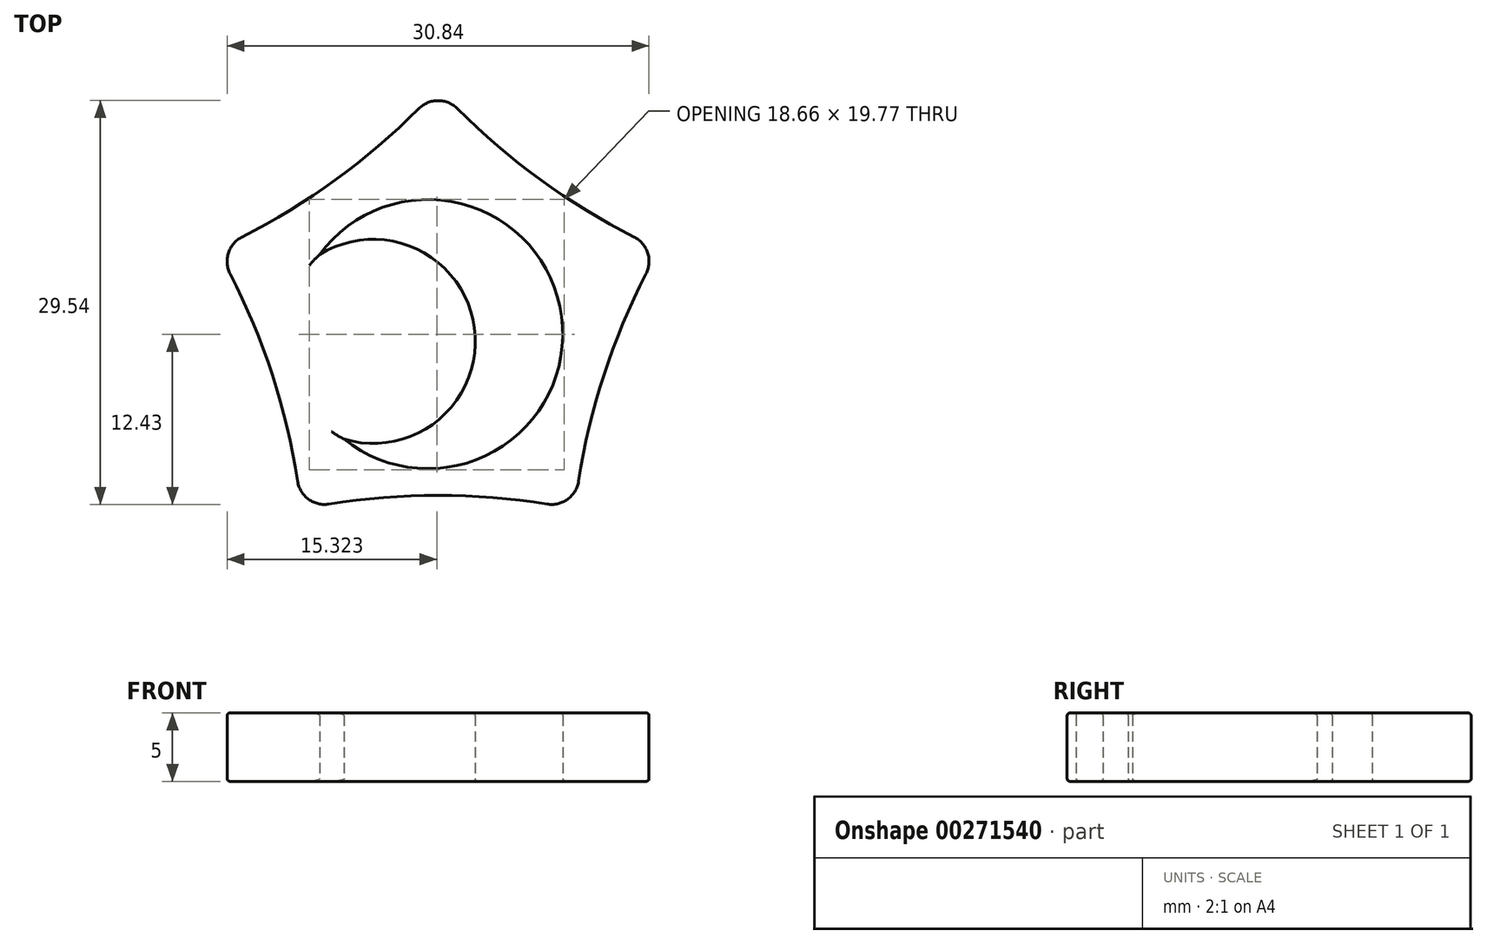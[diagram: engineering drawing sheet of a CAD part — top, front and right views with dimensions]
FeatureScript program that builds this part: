
annotation { "Feature Type Name" : "Feature", "Feature Type Description" : "" }
export const myFeature = defineFeature(function(context is Context, id is Id, definition is map)
    precondition{}
    {
        {
            var Q0;
            Q0=qCreatedBy(makeId("Top.planeOp"),FACE);
            var sketch = newSketch(context, id + "F0", { "sketchPlane" : qUnion([Q0])});
            skCircle(sketch, "E0.cCircle", {"center": v(0, 0) * mm, "radius": 13.76 * mm, "construction": true});
            skLineSegment(sketch, "E0.0", {"start": v(10, -13.76) * mm, "end": v(-10, -13.76) * mm});
            skLineSegment(sketch, "E0.1", {"start": v(-10, -13.76) * mm, "end": v(-16.18, 5.26) * mm});
            skLineSegment(sketch, "E0.2", {"start": v(-16.18, 5.26) * mm, "end": v(0, 17.01) * mm});
            skLineSegment(sketch, "E0.3", {"start": v(0, 17.01) * mm, "end": v(16.18, 5.26) * mm});
            skLineSegment(sketch, "E0.4", {"start": v(16.18, 5.26) * mm, "end": v(10, -13.76) * mm});
            skPoint(sketch, "E0.0.midPoint", {"position": v(0, -13.76) * mm});
            skArc(sketch, "E1", {"start": v(-16.18, 5.26) * mm, "mid": v(-7.5, 10.32) * mm, "end": v(0, 17.01) * mm});
            skArc(sketch, "E2", {"start": v(-10, -13.76) * mm, "mid": v(-12.13, -3.94) * mm, "end": v(-16.18, 5.26) * mm});
            skArc(sketch, "E3", {"start": v(10, -13.76) * mm, "mid": v(0, -12.75) * mm, "end": v(-10, -13.76) * mm});
            skArc(sketch, "E4", {"start": v(16.18, 5.26) * mm, "mid": v(12.13, -3.94) * mm, "end": v(10, -13.76) * mm});
            skArc(sketch, "E5", {"start": v(0, 17.01) * mm, "mid": v(7.5, 10.32) * mm, "end": v(16.18, 5.26) * mm});
            skArc(sketch, "E6", {"start": v(-6.88, -8.65) * mm, "mid": v(9.03, 0.34) * mm, "end": v(-8.67, 4.86) * mm});
            skArc(sketch, "E7", {"start": v(-6.88, -8.65) * mm, "mid": v(2.66, -0.51) * mm, "end": v(-8.67, 4.86) * mm});
            skSolve(sketch);
        }
        {
            var Q0;
            Q0=makeQuery(id+"F0.imprint","IMPRINT",FACE,{"disambiguationData":[TD([[makeQuery(id+"F0.imprint","IMPRINT",EDGE,{"derivedFrom":sQuery(id+"F0.wireOp",EDGE,"E1")}),-1.0]])]});
            extrude(context, id + "F1", {"entities" : qUnion([Q0]), "depth" : 5 * mm});
        }
        {
            var Q0;
            Q0=makeQuery(id+"F1.opExtrude","SWEPT_EDGE",EDGE,{"disambiguationData":[OSD([sQuery(id+"F0.wireOp",EDGE,"E0.1"),sQuery(id+"F0.wireOp",EDGE,"E0.2"),sQuery(id+"F0.wireOp",EDGE,"E1"),sQuery(id+"F0.wireOp",EDGE,"E2")])]});
            var Q1;
            Q1=makeQuery(id+"F1.opExtrude","SWEPT_EDGE",EDGE,{"disambiguationData":[OSD([sQuery(id+"F0.wireOp",EDGE,"E0.2"),sQuery(id+"F0.wireOp",EDGE,"E0.3"),sQuery(id+"F0.wireOp",EDGE,"E1"),sQuery(id+"F0.wireOp",EDGE,"E5")])]});
            var Q2;
            Q2=makeQuery(id+"F1.opExtrude","SWEPT_EDGE",EDGE,{"disambiguationData":[OSD([sQuery(id+"F0.wireOp",EDGE,"E0.3"),sQuery(id+"F0.wireOp",EDGE,"E0.4"),sQuery(id+"F0.wireOp",EDGE,"E4"),sQuery(id+"F0.wireOp",EDGE,"E5")])]});
            var Q3;
            Q3=makeQuery(id+"F1.opExtrude","SWEPT_EDGE",EDGE,{"disambiguationData":[OSD([sQuery(id+"F0.wireOp",EDGE,"E0.0"),sQuery(id+"F0.wireOp",EDGE,"E0.4"),sQuery(id+"F0.wireOp",EDGE,"E3"),sQuery(id+"F0.wireOp",EDGE,"E4")])]});
            var Q4;
            Q4=makeQuery(id+"F1.opExtrude","SWEPT_EDGE",EDGE,{"disambiguationData":[OSD([sQuery(id+"F0.wireOp",EDGE,"E0.0"),sQuery(id+"F0.wireOp",EDGE,"E0.1"),sQuery(id+"F0.wireOp",EDGE,"E2"),sQuery(id+"F0.wireOp",EDGE,"E3")])]});
            fillet(context, id + "F2", {"entities" : qUnion([Q0, Q1, Q2, Q3, Q4]), "radius" : 2 * mm, "tangentPropagation" : true, "allowEdgeOverflow" : false});
        }
        {
            var Q0;
            Q0=makeQuery(id+"F1.opExtrude","CAP_FACE",FACE,{"disambiguationData":[OSD([sQuery(id+"F0.wireOp",EDGE,"E1"),sQuery(id+"F0.wireOp",EDGE,"E2"),sQuery(id+"F0.wireOp",EDGE,"E3"),sQuery(id+"F0.wireOp",EDGE,"E4"),sQuery(id+"F0.wireOp",EDGE,"E5")])],"isStart":false});
            var Q1;
            Q1=makeQuery(id+"F1.opExtrude","CAP_FACE",FACE,{"disambiguationData":[OSD([sQuery(id+"F0.wireOp",EDGE,"E1"),sQuery(id+"F0.wireOp",EDGE,"E2"),sQuery(id+"F0.wireOp",EDGE,"E3"),sQuery(id+"F0.wireOp",EDGE,"E4"),sQuery(id+"F0.wireOp",EDGE,"E5")])],"isStart":true});
            fillet(context, id + "F3", {"entities" : qUnion([Q0, Q1]), "radius" : .2 * mm, "tangentPropagation" : true, "allowEdgeOverflow" : false});
        }
    });
